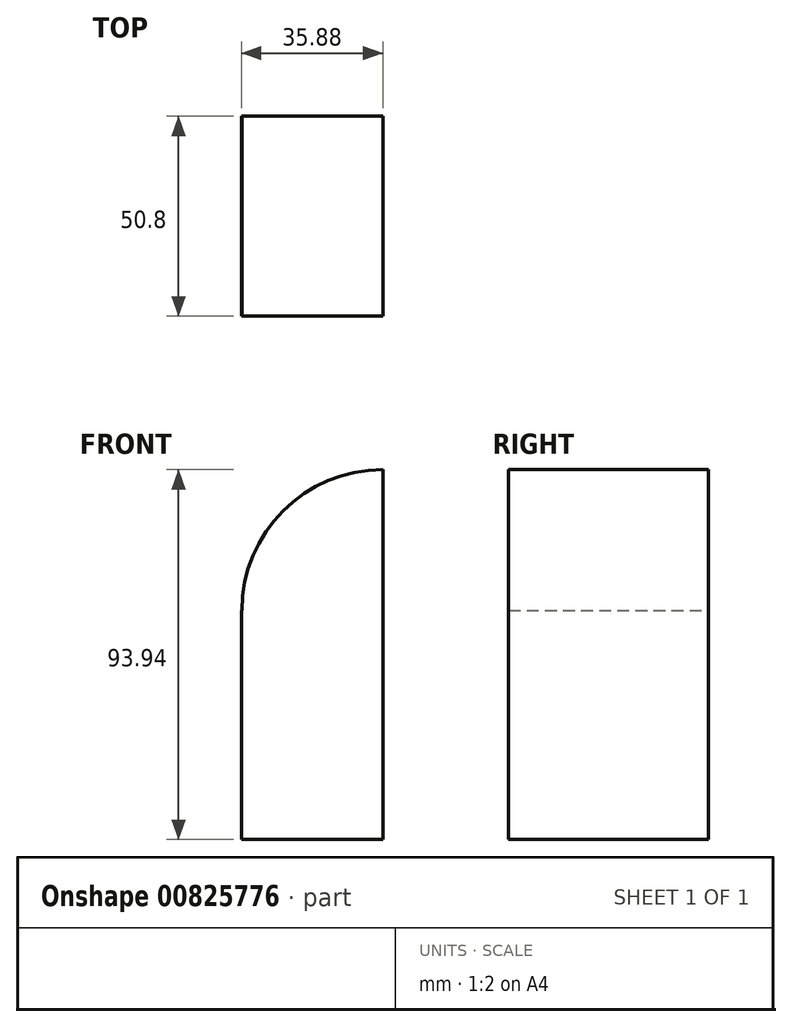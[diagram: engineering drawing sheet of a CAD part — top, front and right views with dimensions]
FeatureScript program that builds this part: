
annotation { "Feature Type Name" : "Feature", "Feature Type Description" : "" }
export const myFeature = defineFeature(function(context is Context, id is Id, definition is map)
    precondition{}
    {
        {
            var Q0;
            Q0=qCreatedBy(makeId("Front.planeOp"),FACE);
            var sketch = newSketch(context, id + "F0", { "sketchPlane" : qUnion([Q0])});
            skArc(sketch, "E0", {"start": v(-35.8, 0) * mm, "mid": v(-25.3, 25.3) * mm, "end": v(0, 35.8) * mm});
            skLineSegment(sketch, "E1", {"start": v(0, 35.8) * mm, "end": v(0, 0) * mm});
            skLineSegment(sketch, "E2.bottom", {"start": v(0, 0) * mm, "end": v(-35.88, 0) * mm});
            skLineSegment(sketch, "E2.top", {"start": v(0, -58.15) * mm, "end": v(-35.88, -58.15) * mm});
            skLineSegment(sketch, "E2.left", {"start": v(0, 0) * mm, "end": v(0, -58.15) * mm});
            skLineSegment(sketch, "E2.right", {"start": v(-35.88, 0) * mm, "end": v(-35.88, -58.15) * mm});
            skSolve(sketch);
        }
        {
            var Q0;
            Q0 = qSketchRegion(id + "F0", true);
            extrude(context, id + "F1", {"entities" : qUnion([Q0]), "depth" : 50.8 * mm, "offsetDistance" : 25.4 * mm});
        }
    });
